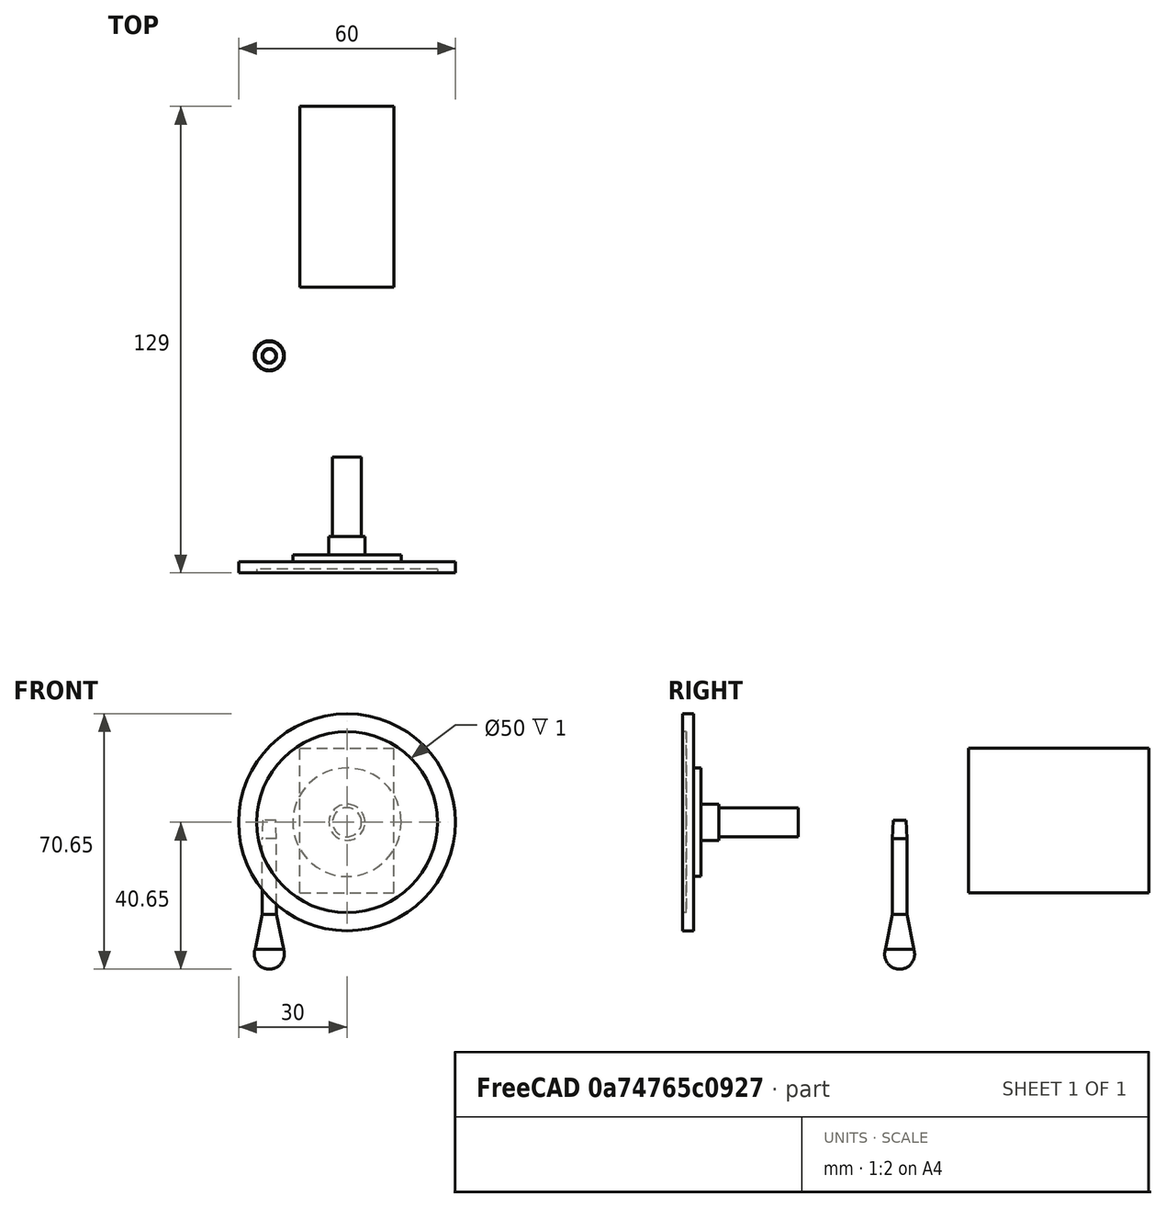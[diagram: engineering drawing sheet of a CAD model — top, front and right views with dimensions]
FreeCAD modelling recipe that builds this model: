
FCSTD DOCUMENT  (FreeCAD 0.16R6662 (Git))
Label: qtippholder-jw-rounded2
License: All rights reserved
LicenseURL: http://en.wikipedia.org/wiki/All_rights_reserved
objects: Part::Cylinder×7, Part::Box×6, Part::Cone×3, Part::MultiFuse×3, Part::Cut×3, Part::Fillet×3, Sketcher::SketchObject×2, App::DocumentObjectGroup×2, Mesh::Feature×1, PartDesign::Pad×1, Part::Sphere×1, PartDesign::Pocket×1
note: 32 computed .brp shape members not serialized (recipe doc carries the construction recipe); baked Part::Feature solids carry a one-line shape summary decoded from their .brp

FEATURE [Mesh::Feature] EarClnrHldr
  Placement = pos=(1.7939,1.69608,-3.31283) rot=(0,0,1;0rad)
FEATURE [Part::Box] Box  label="hut"
  Height = 50
  Length = 36
  Placement = pos=(14,116,11) rot=(0,0,1;0rad)
  Width = 10
FEATURE [Part::Box] Box001  label="stirn"
  Height = 46
  Length = 32
  Placement = pos=(16,102,13) rot=(0,0,1;0rad)
  Width = 17
FEATURE [Part::Box] Box002  label="gnack"
  Height = 10
  Length = 26
  Placement = pos=(22,92,31) rot=(0,0,1;0rad)
  Width = 12
FEATURE [Part::Box] Box003  label="augen"
  Height = 46
  Length = 26
  Placement = pos=(20,77,13) rot=(0,0,1;0rad)
  Width = 26
FEATURE [Part::Box] Box004  label="wangen"
  Height = 35
  Length = 22
  Placement = pos=(22,44,18) rot=(0,0,1;0rad)
  Width = 36
FEATURE [Part::Cylinder] Cylinder  label="kinn"
  Angle = 360
  Height = 18
  Placement = pos=(24,43,35.5) rot=(0,1,0;1.5708rad)
  Radius = 17.5
FEATURE [Sketcher::SketchObject] Sketch001
  Placement = pos=(22,44,36) rot=(0,0,1;0rad)
  sketch-geometry (10):
    g0: LineSegment StartX=1.5 StartY=7.67084 StartZ=0 EndX=-16.9205 EndY=7.67084 EndZ=0
    g1: LineSegment StartX=-20.1462 StartY=11.8885 StartZ=0 EndX=-17.1712 EndY=22.8519 EndZ=0
    g2: LineSegment StartX=-12.6256 StartY=34.6 StartZ=0 EndX=-6.24014 EndY=47.0658 EndZ=0
    g3: LineSegment StartX=-5.70418 StartY=49.2877 StartZ=0 EndX=-5.70418 EndY=58.874 EndZ=0
    g4: LineSegment StartX=-5.70418 StartY=58.874 StartZ=0 EndX=1.5 EndY=58.874 EndZ=0
    g5: LineSegment StartX=1.5 StartY=58.874 StartZ=0 EndX=1.5 EndY=7.67084 EndZ=0
    g6: ArcOfCircle CenterX=-16.9205 CenterY=11.0132 CenterZ=0 NormalX=0 NormalY=0 NormalZ=1 Radius=3.34236 StartAngle=2.87662 EndAngle=4.71239
    g7: ArcOfCircle CenterX=41.2664 CenterY=6.99453 CenterZ=0 NormalX=0 NormalY=0 NormalZ=1 Radius=60.5508 StartAngle=2.6682 EndAngle=2.87662
    g8: ArcOfCircle CenterX=-10.5778 CenterY=49.2877 CenterZ=0 NormalX=0 NormalY=0 NormalZ=1 Radius=4.87365 StartAngle=5.8098 EndAngle=6.28319
    g9: Circle CenterX=-11.5 CenterY=17.6445 CenterZ=0 NormalX=0 NormalY=0 NormalZ=1 Radius=1.5
  constraints (14):
    c: Horizontal(g0)
    c: Vertical(g3)
    c: Coincident(g3,g4)
    c: Horizontal(g4)
    c: Coincident(g4,g5)
    c: Coincident(g5,g0)
    c: Vertical(g5)
    c: Tangent(g0,g6) = 1.5708
    c: Tangent(g1,g6) = 1.5708
    c: Tangent(g1,g7) = 1.5708
    c: Tangent(g2,g7) = 1.5708
    c: Tangent(g2,g8) = -1.5708
    c: Tangent(g3,g8) = -1.5708
    c: Radius(g9) = 1.5
FEATURE [PartDesign::Pad] Pad  label="nase"
  Length = 4.5
  Length2 = 5.5
  Placement = pos=(22,44,36) rot=(0,0,1;0rad)
  Sketch = -> Sketch001
  Type = 4
FEATURE [Part::Cylinder] Cylinder002  label="bein006"
  Angle = 360
  Height = 32
  Placement = pos=(32,34,35.5) rot=(1,0,0;1.5708rad)
  Radius = 4
FEATURE [Part::Cylinder] Cylinder003  label="bein001"
  Angle = 360
  Height = 11
  Placement = pos=(32,12,35.5) rot=(1,0,0;1.5708rad)
  Radius = 5
FEATURE [Part::Cylinder] Cylinder004  label="bein002"
  Angle = 360
  Height = 4
  Placement = pos=(32,7,35.5) rot=(1,0,0;1.5708rad)
  Radius = 15
FEATURE [Part::Cylinder] Cylinder005  label="bein003"
  Angle = 360
  Height = 3
  Placement = pos=(32,5,35.5) rot=(1,0,0;1.5708rad)
  Radius = 30
FEATURE [Part::Cylinder] Cylinder006  label="bein004"
  Angle = 360
  Height = 3
  Placement = pos=(32,3,35.5) rot=(1,0,0;1.5708rad)
  Radius = 25
FEATURE [Part::Box] Box005  label="kopfloch"
  Height = 40
  Length = 26
  Placement = pos=(19,81,16) rot=(0,0,1;0rad)
  Width = 50
FEATURE [Part::Cylinder] Cylinder007  label="staebchen"
  Angle = 360
  Height = 27
  Placement = pos=(10.5,62,4) rot=(0,0,1;0rad)
  Radius = 2
FEATURE [Part::Sphere] Sphere  label="Kugel"
  Angle1 = -90
  Angle2 = 90
  Angle3 = 360
  Placement = pos=(10.5,62,-1) rot=(0,0,1;0rad)
  Radius = 4.15
FEATURE [Part::Cone] Cone  label="Kegel"
  Angle = 360
  Height = 10
  Placement = pos=(10.5,62,0) rot=(0,0,1;0rad)
  Radius1 = 4
  Radius2 = 2
FEATURE [Part::Cone] Cone001  label="Kegel001"
  Angle = 360
  Height = 5
  Placement = pos=(10.5,62,31) rot=(0,0,1;0rad)
  Radius1 = 2
  Radius2 = 1.8
FEATURE [Part::Cone] Cone002  label="beinloch001"
  Angle = 360
  Height = 11
  Placement = pos=(32,35,35.5) rot=(1,0,0;1.5708rad)
  Radius1 = 3.9
  Radius2 = 4.2
FEATURE [Part::MultiFuse] Fusion
  Shapes = -> [Box,Box001,Box002,Box003,Box004,Cylinder,Pad]
FEATURE [Part::MultiFuse] Fusion001
  Shapes = -> [Cone001,Cylinder007,Sphere,Cone]
FEATURE [App::DocumentObjectGroup] Gruppe001  label="halb-qtipp"
  Group = -> [Fusion001]
FEATURE [Part::MultiFuse] Fusion002
  Shapes = -> [Cylinder002,Cylinder003,Cylinder005,Cylinder004]
FEATURE [Part::Cut] Cut002
  Base = -> Fusion002
  Tool = -> Cylinder006
FEATURE [App::DocumentObjectGroup] Gruppe  label="bein"
  Group = -> [Cut002]
FEATURE [Sketcher::SketchObject] Sketch
  Placement = pos=(19,81,16) rot=(1,0,0;3.14159rad)
  Support = -> Box005 [Face5]
  sketch-geometry (4):
    g0: LineSegment StartX=0 StartY=0 StartZ=0 EndX=0 EndY=-1 EndZ=0
    g1: LineSegment StartX=0 StartY=-1 StartZ=0 EndX=2 EndY=-1 EndZ=0
    g2: LineSegment StartX=2 StartY=-1 StartZ=0 EndX=4 EndY=0 EndZ=0
    g3: LineSegment StartX=4 StartY=0 StartZ=0 EndX=0 EndY=0 EndZ=0
  constraints (11):
    c: Coincident(g-1,g0)
    c: PointOnObject(g0,g-2)
    c: Coincident(g0,g1)
    c: Horizontal(g1)
    c: Coincident(g1,g2)
    c: Coincident(g2,g3)
    c: Coincident(g3,g0)
    c: Horizontal(g3)
    c: DistanceY(g0,g0) = 1
    c: DistanceX(g1,g1) = 2
    c: DistanceX(g3,g3) = 4
FEATURE [PartDesign::Pocket] Pocket
  Length = 5
  Placement = pos=(19,81,16) rot=(0,0,1;0rad)
  Sketch = -> Sketch
  Type = 1
FEATURE [Part::Cut] Cut
  Base = -> Fusion
  Tool = -> Pocket
FEATURE [Part::Cut] Cut003  label="kopf"
  Base = -> Cut
  Tool = -> Cone002
FEATURE [Part::Fillet] Fillet
  Base = -> Cut003
  Edges = 14 edges r=4: [Edge90,Edge91,Edge92,Edge93,Edge94,Edge95,Edge96,Edge111,Edge119,Edge120,Edge123,Edge125,Edge126,Edge127]
FEATURE [Part::Fillet] Fillet001
  Base = -> Fillet
  Edges = 16 edges r=2: [Edge44,Edge50,Edge57,Edge116,Edge117,Edge118,Edge119,Edge120,Edge136,Edge137,Edge138,Edge139,Edge163,Edge164,Edge165,Edge166]
FEATURE [Part::Fillet] Fillet002
  Base = -> Fillet001
  Edges = 15 edges r=1: [Edge36,Edge54,Edge65,Edge85,Edge94,Edge96,Edge98,Edge99,Edge100,Edge101,Edge102,Edge103,Edge162,Edge230,Edge231]
